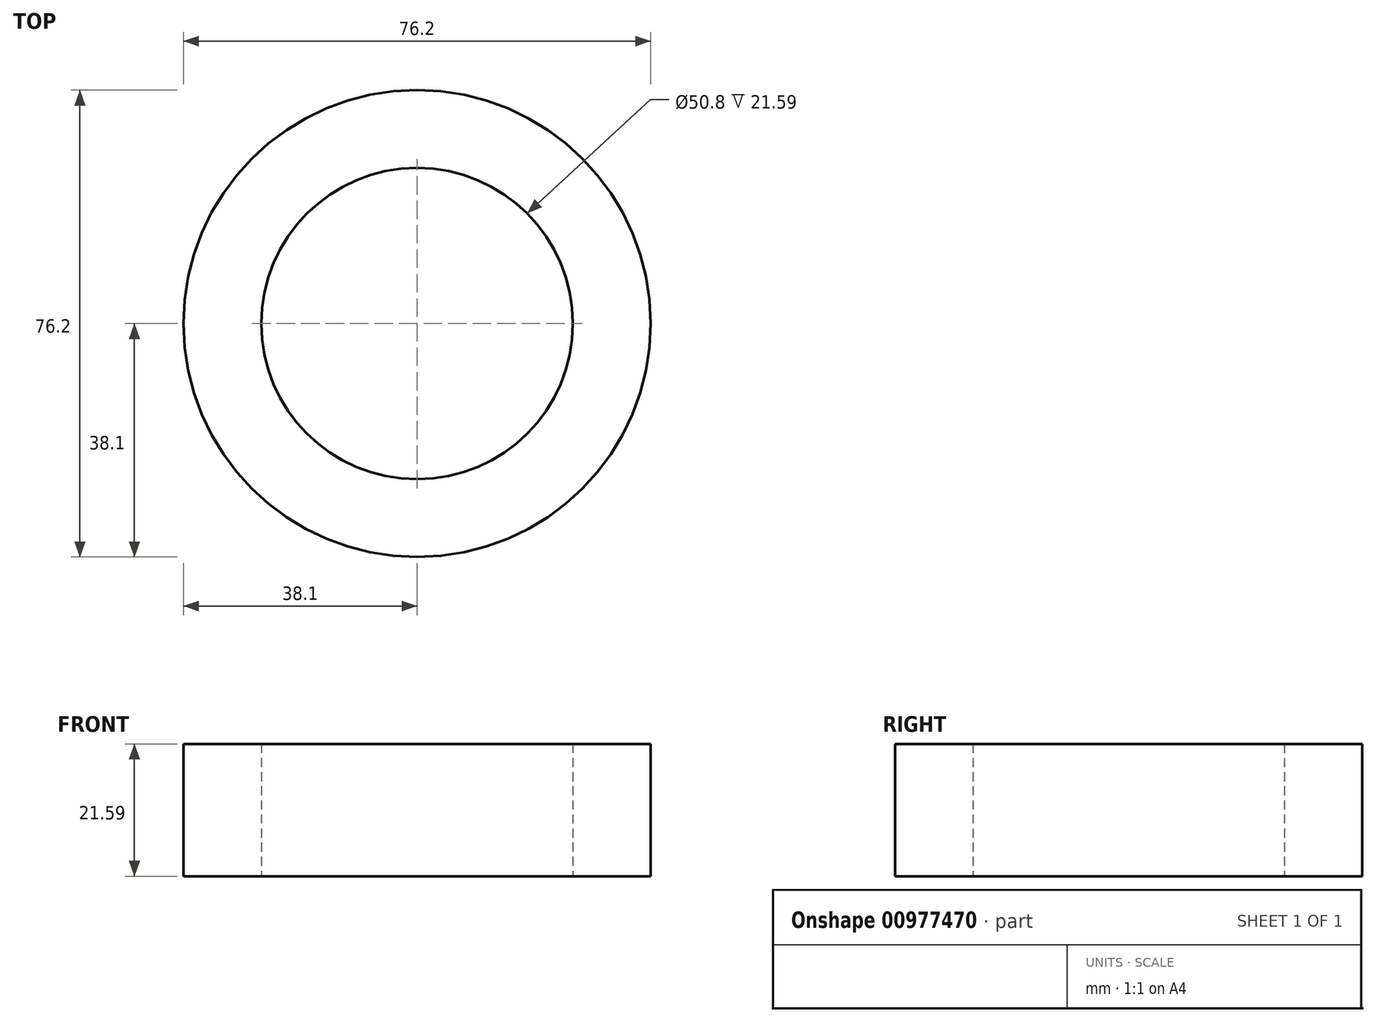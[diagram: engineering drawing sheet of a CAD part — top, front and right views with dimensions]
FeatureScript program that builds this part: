
annotation { "Feature Type Name" : "Feature", "Feature Type Description" : "" }
export const myFeature = defineFeature(function(context is Context, id is Id, definition is map)
    precondition{}
    {
        {
            var Q0;
            Q0=qCreatedBy(makeId("Top.planeOp"),FACE);
            var sketch = newSketch(context, id + "F0", { "sketchPlane" : qUnion([Q0])});
            skCircle(sketch, "E0", {"center": v(0, 0) * mm, "radius": 25.4 * mm});
            skCircle(sketch, "E1", {"center": v(0, 0) * mm, "radius": 38.1 * mm});
            skSolve(sketch);
        }
        {
            var Q0;
            Q0 = qSketchRegion(id + "F0", true);
            extrude(context, id + "F1", {"entities" : qUnion([Q0]), "depth" : 21.59 * mm, "offsetDistance" : 25.4 * mm});
        }
    });
